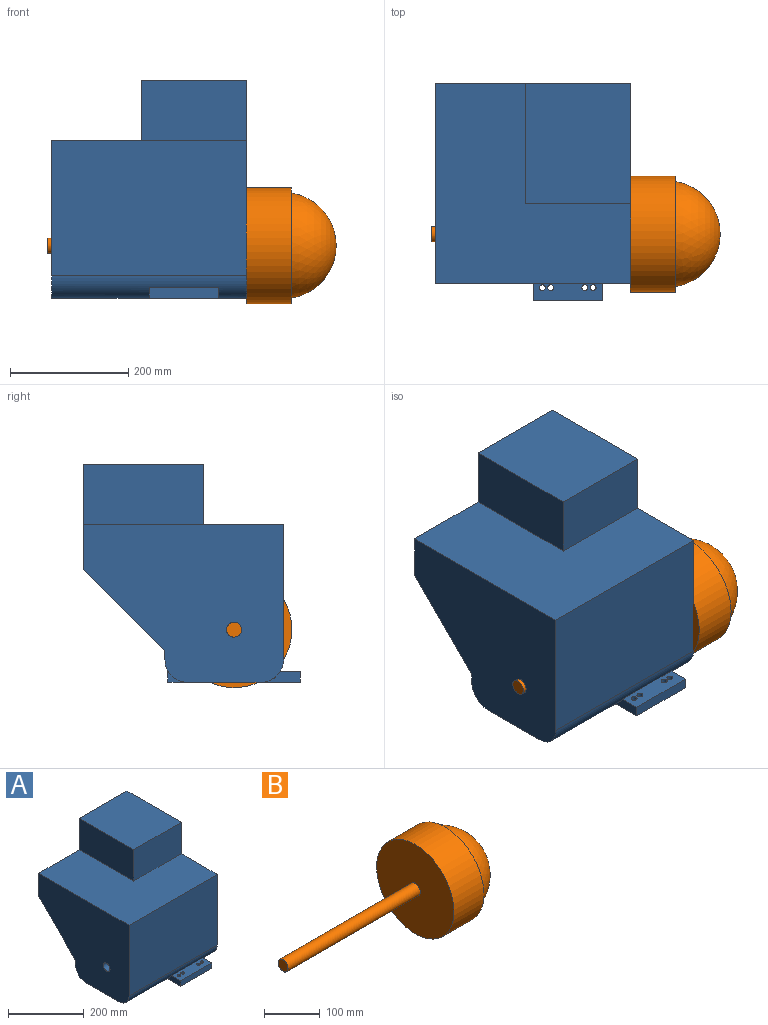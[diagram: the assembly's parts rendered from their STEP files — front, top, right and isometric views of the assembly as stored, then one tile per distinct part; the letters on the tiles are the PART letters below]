
ASSEMBLY  parts=2 mates=1
PART A: 34 faces, bbox 330.2x365.9x368.3 mm
  f0: plane 203.2x177.8mm, normal (0,0,1), area 36129mm2, adj f2,f3,f8,f10
  f1: plane 330.2x137.16mm, normal (0,0.71,-0.71), area 64050.1mm2, adj f2,f7,f8,f9
  f2: plane 330.2x177.8mm, normal (0,1,0), area 43225.7mm2, adj f0,f1,f4,f8,f9,f10
  f3: plane 177.8x101.6mm, normal (0,-1,0), area 18064.5mm2, adj f0,f4,f8,f10
  f4: plane 337.82x330.2mm, normal (0,0,1), area 75419.2mm2, adj f2,f3,f5,f8,f9,f10
  f5: plane 330.2x228.6mm, normal (0,-1,0), area 75483.7mm2, adj f4,f8,f9,f12
  f6: plane 330.2x223.77mm, normal (0,0,-1), area 52072.2mm2, adj f8,f9,f12,f13,f14,f15,f16,f17
  f7: plane 330.2x15.24mm, normal (0,1,0), area 5032.2mm2, adj f1,f8,f9,f13
  f8: plane 368.3x337.82mm, normal (1,0,0), area 92889.4mm2, adj f0,f1,f2,f3,f4,f5,f6,f7
  f9: plane 337.82x266.7mm, normal (-1,0,0), area 72244.3mm2, adj f1,f2,f4,f5,f6,f7,f11,f12
  f10: plane 203.2x101.6mm, normal (-1,0,0), area 20645.1mm2, adj f0,f2,f3,f4
  f11: cylinder r=12.7mm len=330.2mm, axis (1,0,0), area 26348.8mm2, adj f8,f9
  f12: cylinder r=38.1mm len=330.2mm, axis (1,0,0), area 15273.2mm2, adj f5,f6,f8,f9,f15,f20,f21
  f13: cylinder r=38.1mm len=330.2mm, axis (-1,0,0), area 15273.2mm2, adj f6,f7,f8,f9,f22,f28,f29
  f14: plane 116.84x17.78mm, normal (0,-1,0), area 2077.4mm2, adj f6,f15,f20,f21
  f15: plane 66.17x17.78mm, normal (-1,0,0), area 772.1mm2, adj f6,f12,f14,f21
  f16: cylinder r=5mm len=17.78mm, axis (0,0,-1), area 558.6mm2, adj f6,f21
  f17: cylinder r=5mm len=17.78mm, axis (0,0,-1), area 558.6mm2, adj f6,f21
  f18: cylinder r=5mm len=17.78mm, axis (0,0,-1), area 558.6mm2, adj f6,f21
  f19: cylinder r=5mm len=17.78mm, axis (0,0,-1), area 558.6mm2, adj f6,f21
  f20: plane 66.17x17.78mm, normal (1,0,0), area 772.1mm2, adj f6,f12,f14,f21
  f21: plane 116.84x33.94mm, normal (0,0,1), area 3651.2mm2, adj f12,f14,f15,f16,f17,f18,f19,f20
  f22: plane 33.15x17.78mm, normal (-1,0,0), area 185mm2, adj f6,f13,f23,f29
  f23: plane 116.84x17.78mm, normal (0,1,0), area 2077.4mm2, adj f6,f22,f28,f29
  f24: cylinder r=5mm len=17.78mm, axis (0,0,-1), area 558.6mm2, adj f6,f30
  f25: cylinder r=5mm len=17.78mm, axis (0,0,-1), area 558.6mm2, adj f6,f31
  f26: cylinder r=5mm len=17.78mm, axis (0,0,-1), area 558.6mm2, adj f6,f32
  f27: cylinder r=5mm len=17.78mm, axis (0,0,-1), area 558.6mm2, adj f6,f33
  f28: plane 33.15x17.78mm, normal (1,0,0), area 185mm2, adj f6,f13,f23,f29
  f29: plane 116.84x0.92mm, normal (0,0,1), area 107.3mm2, adj f13,f22,f23,f28
  f30: plane 10x10mm, normal (0,0,-1), area 78.5mm2, adj f24
  f31: plane 10x10mm, normal (0,0,-1), area 78.5mm2, adj f25
  f32: plane 10x10mm, normal (0,0,-1), area 78.5mm2, adj f26
  f33: plane 10x10mm, normal (0,0,-1), area 78.5mm2, adj f27
PART B: 6 faces, bbox 487.7x196x196 mm
  f0: cylinder r=98mm len=196mm, axis (-1,0,0), area 46920.3mm2, adj f1,f2
  f1: plane 196x196mm, normal (1,0,0), area 5343.2mm2, adj f0,f3
  f2: plane 196x196mm, normal (-1,0,0), area 29665.1mm2, adj f0,f4
  f3: sphere r=89.96mm, area 43070.1mm2, adj f1
  f4: cylinder r=12.7mm len=335.28mm, axis (-1,0,0), area 26754.2mm2, adj f2,f5
  f5: plane 25.4x25.4mm, normal (-1,0,0), area 506.7mm2, adj f4
PLACE A at identity fixed
PLACE B rot(axis=(1,0,0),29.2deg) t=(-3.81,0,0)mm
MATE revolute A.f11 <-> B.f4  axis (-1,0,0) through (-165.1,0,0)mm
